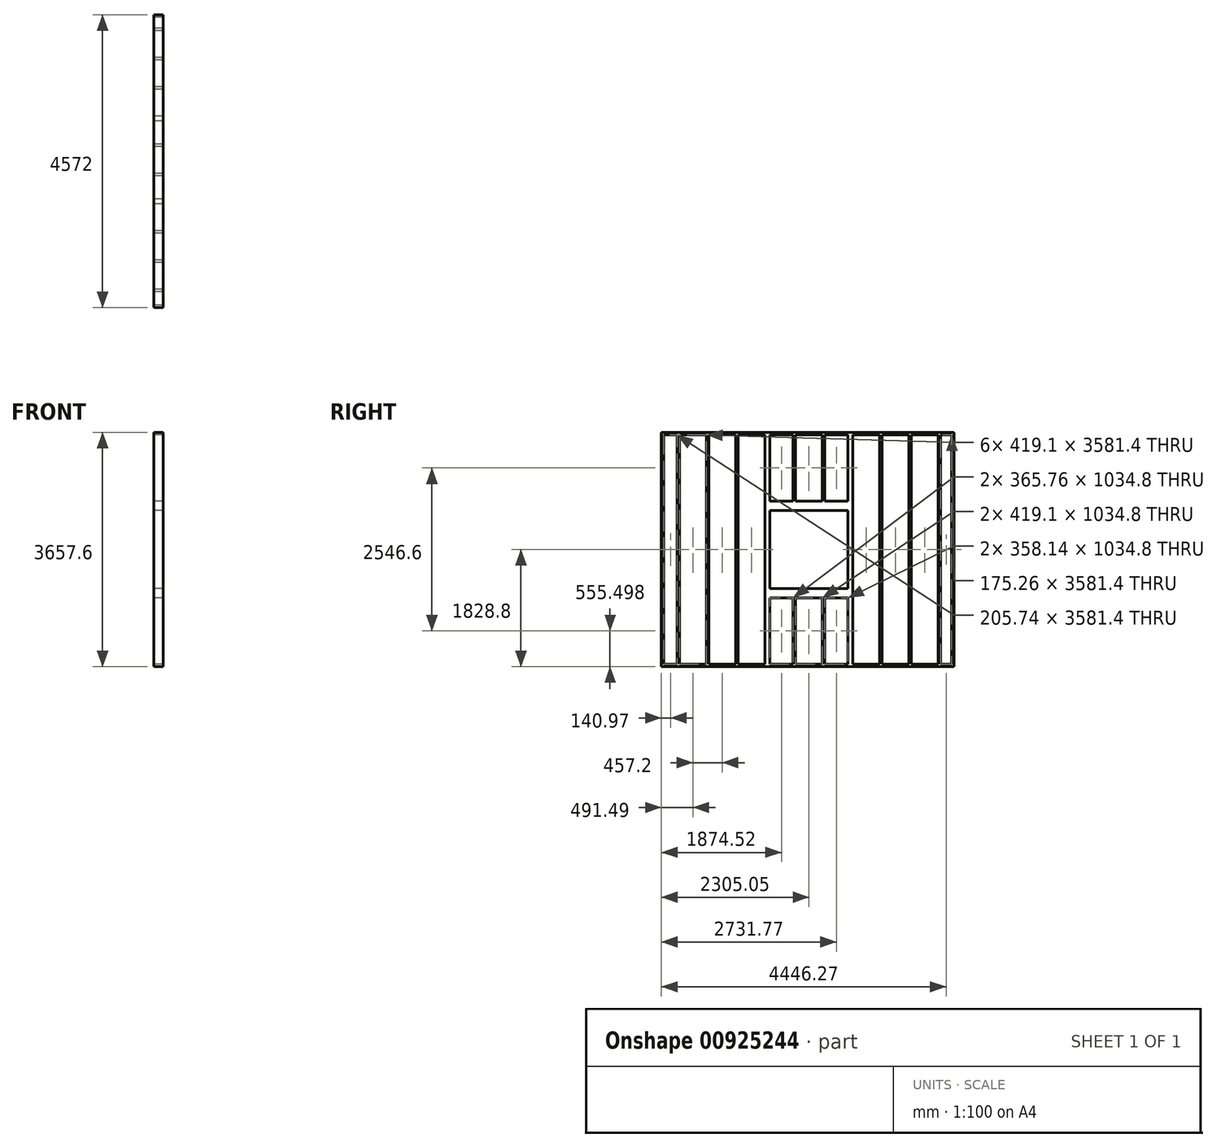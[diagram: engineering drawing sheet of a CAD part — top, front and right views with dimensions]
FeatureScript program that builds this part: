
annotation { "Feature Type Name" : "Feature", "Feature Type Description" : "" }
export const myFeature = defineFeature(function(context is Context, id is Id, definition is map)
    precondition{}
    {
        {
            var Q0;
            Q0=qCreatedBy(makeId("Right.planeOp"),FACE);
            var sketch = newSketch(context, id + "F0", { "sketchPlane" : qUnion([Q0])});
            skLineSegment(sketch, "E0.bottom", {"start": v(0, 0) * mm, "end": v(4572, 0) * mm});
            skLineSegment(sketch, "E0.top", {"start": v(0, 3657.6) * mm, "end": v(4572, 3657.6) * mm});
            skLineSegment(sketch, "E1.8.0.0", {"start": v(243.84, 3619.5) * mm, "end": v(243.84, 38.1) * mm});
            skLineSegment(sketch, "E1.8.0.1", {"start": v(281.94, 3619.5) * mm, "end": v(281.94, 38.1) * mm});
            skLineSegment(sketch, "E1.9.0.0", {"start": v(701.04, 3619.5) * mm, "end": v(701.04, 38.1) * mm});
            skLineSegment(sketch, "E1.9.0.1", {"start": v(739.14, 3619.5) * mm, "end": v(739.14, 38.1) * mm});
            skLineSegment(sketch, "E1.10.0.0", {"start": v(1158.24, 3619.5) * mm, "end": v(1158.24, 38.1) * mm});
            skLineSegment(sketch, "E1.10.0.1", {"start": v(1196.34, 3619.5) * mm, "end": v(1196.34, 38.1) * mm});
            skLineSegment(sketch, "E1.11.0.0", {"start": v(1615.44, 3619.5) * mm, "end": v(1615.44, 38.1) * mm});
            skLineSegment(sketch, "E1.11.0.1", {"start": v(1691.64, 3619.5) * mm, "end": v(1691.64, 2584.7) * mm});
            skLineSegment(sketch, "E1.12.0.0", {"start": v(2057.4, 3619.5) * mm, "end": v(2057.4, 2584.7) * mm});
            skLineSegment(sketch, "E1.12.0.1", {"start": v(2095.5, 3619.5) * mm, "end": v(2095.5, 2584.7) * mm});
            skLineSegment(sketch, "E1.13.0.0", {"start": v(2514.6, 3619.5) * mm, "end": v(2514.6, 2584.7) * mm});
            skLineSegment(sketch, "E1.13.0.1", {"start": v(2552.7, 3619.5) * mm, "end": v(2552.7, 2584.7) * mm});
            skLineSegment(sketch, "E1.14.0.0", {"start": v(2910.84, 3619.5) * mm, "end": v(2910.84, 2584.7) * mm});
            skLineSegment(sketch, "E1.14.0.1", {"start": v(2987.04, 3619.5) * mm, "end": v(2987.04, 38.1) * mm});
            skLineSegment(sketch, "E1.15.0.0", {"start": v(3406.14, 3619.5) * mm, "end": v(3406.14, 38.1) * mm});
            skLineSegment(sketch, "E1.15.0.1", {"start": v(3444.24, 3619.5) * mm, "end": v(3444.24, 38.1) * mm});
            skLineSegment(sketch, "E1.16.0.0", {"start": v(3863.34, 3619.5) * mm, "end": v(3863.34, 38.1) * mm});
            skLineSegment(sketch, "E1.16.0.1", {"start": v(3901.44, 3619.5) * mm, "end": v(3901.44, 38.1) * mm});
            skLineSegment(sketch, "E1.17.0.0", {"start": v(4320.54, 3619.5) * mm, "end": v(4320.54, 38.1) * mm});
            skLineSegment(sketch, "E1.17.0.1", {"start": v(4358.64, 3619.5) * mm, "end": v(4358.64, 38.1) * mm});
            skLineSegment(sketch, "E2.trimOffspring", {"start": v(38.1, 3619.5) * mm, "end": v(243.84, 3619.5) * mm});
            skLineSegment(sketch, "E3.trimOffspring", {"start": v(281.94, 3619.5) * mm, "end": v(701.04, 3619.5) * mm});
            skLineSegment(sketch, "E4.trimOffspring", {"start": v(739.14, 3619.5) * mm, "end": v(1158.24, 3619.5) * mm});
            skLineSegment(sketch, "E5.trimOffspring", {"start": v(1196.34, 3619.5) * mm, "end": v(1615.44, 3619.5) * mm});
            skLineSegment(sketch, "E6.trimOffspring", {"start": v(1691.64, 3619.5) * mm, "end": v(2057.4, 3619.5) * mm});
            skLineSegment(sketch, "E7.trimOffspring", {"start": v(2095.5, 3619.5) * mm, "end": v(2514.6, 3619.5) * mm});
            skLineSegment(sketch, "E8.trimOffspring", {"start": v(2552.7, 3619.5) * mm, "end": v(2910.84, 3619.5) * mm});
            skLineSegment(sketch, "E9.trimOffspring", {"start": v(2987.04, 3619.5) * mm, "end": v(3406.14, 3619.5) * mm});
            skLineSegment(sketch, "E10.trimOffspring", {"start": v(3444.24, 3619.5) * mm, "end": v(3863.34, 3619.5) * mm});
            skLineSegment(sketch, "E11.trimOffspring", {"start": v(3901.44, 3619.5) * mm, "end": v(4320.54, 3619.5) * mm});
            skLineSegment(sketch, "E12.trimOffspring", {"start": v(4358.64, 3619.5) * mm, "end": v(4572, 3619.5) * mm});
            skLineSegment(sketch, "E13.trimOffspring", {"start": v(4358.64, 38.1) * mm, "end": v(4533.9, 38.1) * mm});
            skLineSegment(sketch, "E14.trimOffspring", {"start": v(3901.44, 38.1) * mm, "end": v(4320.54, 38.1) * mm});
            skLineSegment(sketch, "E15.trimOffspring", {"start": v(3444.24, 38.1) * mm, "end": v(3863.34, 38.1) * mm});
            skLineSegment(sketch, "E16.trimOffspring", {"start": v(2987.04, 38.1) * mm, "end": v(3406.14, 38.1) * mm});
            skLineSegment(sketch, "E17.trimOffspring", {"start": v(2552.7, 38.1) * mm, "end": v(2910.84, 38.1) * mm});
            skLineSegment(sketch, "E18.trimOffspring", {"start": v(2095.5, 38.1) * mm, "end": v(2514.6, 38.1) * mm});
            skLineSegment(sketch, "E19.trimOffspring", {"start": v(1691.64, 38.1) * mm, "end": v(2057.4, 38.1) * mm});
            skLineSegment(sketch, "E20.trimOffspring", {"start": v(1196.34, 38.1) * mm, "end": v(1615.44, 38.1) * mm});
            skLineSegment(sketch, "E21.trimOffspring", {"start": v(739.14, 38.1) * mm, "end": v(1158.24, 38.1) * mm});
            skLineSegment(sketch, "E22.trimOffspring", {"start": v(281.94, 38.1) * mm, "end": v(701.04, 38.1) * mm});
            skLineSegment(sketch, "E23.trimOffspring", {"start": v(38.1, 38.1) * mm, "end": v(243.84, 38.1) * mm});
            skLineSegment(sketch, "E24.bottom", {"start": v(1691.64, 2438.4) * mm, "end": v(2057.4, 2438.4) * mm});
            skLineSegment(sketch, "E24.top", {"start": v(1691.64, 1219.2) * mm, "end": v(2552.7, 1219.2) * mm});
            skLineSegment(sketch, "E24.left", {"start": v(1691.64, 2438.4) * mm, "end": v(1691.64, 1219.2) * mm});
            skLineSegment(sketch, "E24.right", {"start": v(2910.84, 2438.4) * mm, "end": v(2910.84, 1219.2) * mm});
            skLineSegment(sketch, "E25.trimOffspring", {"start": v(1691.64, 1072.9) * mm, "end": v(1691.64, 38.1) * mm});
            skLineSegment(sketch, "E26.trimOffspring", {"start": v(2910.84, 1072.9) * mm, "end": v(2910.84, 38.1) * mm});
            skLineSegment(sketch, "E27", {"start": v(1691.64, 1072.9) * mm, "end": v(2057.4, 1072.9) * mm});
            skLineSegment(sketch, "E28", {"start": v(1691.64, 2584.7) * mm, "end": v(2057.4, 2584.7) * mm});
            skLineSegment(sketch, "E29.trimOffspring", {"start": v(2057.4, 1072.9) * mm, "end": v(2057.4, 38.1) * mm});
            skLineSegment(sketch, "E30.trimOffspring", {"start": v(2095.5, 1072.9) * mm, "end": v(2095.5, 38.1) * mm});
            skLineSegment(sketch, "E31.trimOffspring", {"start": v(2514.6, 1072.9) * mm, "end": v(2514.6, 38.1) * mm});
            skLineSegment(sketch, "E32.trimOffspring", {"start": v(2552.7, 1072.9) * mm, "end": v(2552.7, 38.1) * mm});
            skLineSegment(sketch, "E33.trimOffspring", {"start": v(2095.5, 1219.2) * mm, "end": v(2514.6, 1219.2) * mm});
            skLineSegment(sketch, "E34.trimOffspring", {"start": v(2095.5, 1072.9) * mm, "end": v(2514.6, 1072.9) * mm});
            skLineSegment(sketch, "E35.trimOffspring", {"start": v(2552.7, 1219.2) * mm, "end": v(2910.84, 1219.2) * mm});
            skLineSegment(sketch, "E36.trimOffspring", {"start": v(2552.7, 1072.9) * mm, "end": v(2910.84, 1072.9) * mm});
            skLineSegment(sketch, "E37.trimOffspring", {"start": v(2095.5, 2584.7) * mm, "end": v(2514.6, 2584.7) * mm});
            skLineSegment(sketch, "E38.trimOffspring", {"start": v(2552.7, 2584.7) * mm, "end": v(2910.84, 2584.7) * mm});
            skLineSegment(sketch, "E39.trimOffspring", {"start": v(2057.4, 2438.4) * mm, "end": v(2552.7, 2438.4) * mm});
            skLineSegment(sketch, "E40.trimOffspring", {"start": v(2552.7, 2438.4) * mm, "end": v(2910.84, 2438.4) * mm});
            skLineSegment(sketch, "E41", {"start": v(2057.4, 2438.4) * mm, "end": v(2514.6, 2438.4) * mm});
            skLineSegment(sketch, "E42", {"start": v(0, 3657.6) * mm, "end": v(0, 0) * mm});
            skLineSegment(sketch, "E43", {"start": v(38.1, 38.1) * mm, "end": v(38.1, 3619.5) * mm});
            skLineSegment(sketch, "E44", {"start": v(4533.9, 3619.5) * mm, "end": v(4533.9, 38.1) * mm});
            skLineSegment(sketch, "E45", {"start": v(4572, 3619.5) * mm, "end": v(4572, 38.1) * mm});
            skLineSegment(sketch, "E46", {"start": v(4572, 3619.5) * mm, "end": v(4572, 3657.6) * mm});
            skLineSegment(sketch, "E47", {"start": v(4572, 38.1) * mm, "end": v(4572, 0) * mm});
            skSolve(sketch);
        }
        {
            var Q0;
            Q0=qSketchRegion(id+"F0",true);
            extrude(context, id + "F1", {"entities" : qUnion([Q0]), "depth" : 146.3 * mm, "offsetDistance" : 30.48 * mm});
        }
    });
